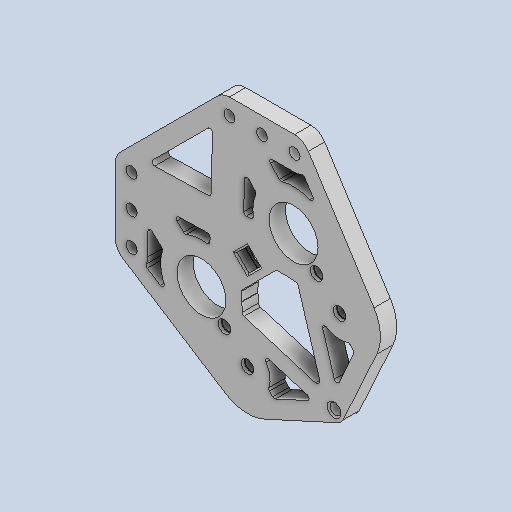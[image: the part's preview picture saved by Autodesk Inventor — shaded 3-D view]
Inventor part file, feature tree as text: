
AUTODESK INVENTOR PART (.ipt)
format: ipt  version: 2022 (Build 260153000, 153)  size: 371,200 bytes
history: native  units: in
note: dims shown in document units (in); Inventor stores cm internally (conversion verified against a paired STEP export)
features: sketch x5, other x3
ambient origin geometry x8: Origin, YZ Plane, XZ Plane, XY Plane, X Axis, Y Axis, Z Axis, Center Point
bodies: Solid1 (feature_tree)
feature tree (8):
  other  "motorplate_MIR.ipt"
  other  "Solid1::motorplate_MIR.ipt"
  other  "TaggingFeature1"
  sketch  "Sketch1"  dims[d0=0.3937in]
  sketch  "Sketch2"
  sketch  "Sketch3"
  sketch  "Sketch4"
  sketch  "Sketch5"
